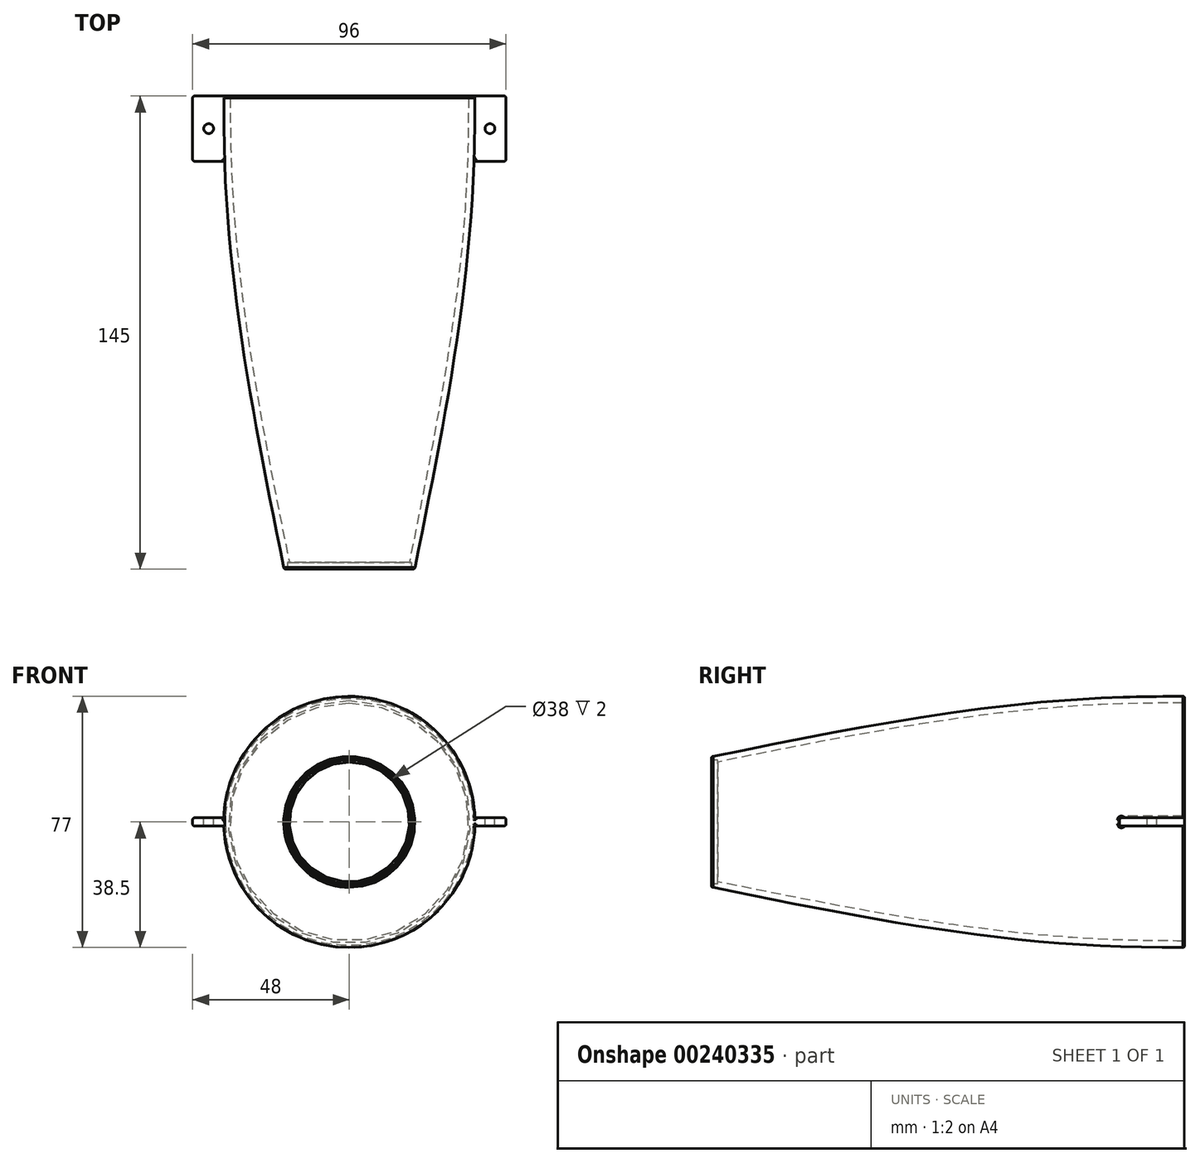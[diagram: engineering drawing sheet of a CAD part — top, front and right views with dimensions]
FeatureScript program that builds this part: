
annotation { "Feature Type Name" : "Feature", "Feature Type Description" : "" }
export const myFeature = defineFeature(function(context is Context, id is Id, definition is map)
    precondition{}
    {
        {
            var Q0;
            Q0=qCreatedBy(makeId("Front.planeOp"),FACE);
            var sketch = newSketch(context, id + "F0", { "sketchPlane" : qUnion([Q0])});
            skCircle(sketch, "E0", {"center": v(0, 0) * mm, "radius": 38.5 * mm});
            skSolve(sketch);
        }
        {
            var Q0;
            Q0=qCreatedBy(makeId("Front.planeOp"),FACE);
            cPlane(context, id + "F1", {"entities" : qUnion([Q0]), "cplaneType" : CPlaneType.OFFSET, "offset" : 20 * mm, "width" : 150 * mm, "height" : 150 * mm});
        }
        {
            var Q0;
            Q0=qCreatedBy(id+"F1.planeOp",FACE);
            var sketch = newSketch(context, id + "F2", { "sketchPlane" : qUnion([Q0])});
            skCircle(sketch, "E1", {"center": v(0, 0) * mm, "radius": 38.2 * mm});
            skSolve(sketch);
        }
        {
            var Q0;
            Q0=qCreatedBy(id+"F1.planeOp",FACE);
            cPlane(context, id + "F3", {"entities" : qUnion([Q0]), "cplaneType" : CPlaneType.OFFSET, "offset" : 125 * mm, "width" : 150 * mm, "height" : 150 * mm});
        }
        {
            var Q0;
            Q0=qCreatedBy(id+"F3.planeOp",FACE);
            var sketch = newSketch(context, id + "F4", { "sketchPlane" : qUnion([Q0])});
            skCircle(sketch, "E2", {"center": v(0, 0) * mm, "radius": 20 * mm});
            skSolve(sketch);
        }
        {
            var Q0;
            Q0 = qSketchRegion(id + "F0", true);
            var Q1;
            Q1 = qSketchRegion(id + "F2", true);
            var Q2;
            Q2 = qSketchRegion(id + "F4", true);
            loft(context, id + "F5", {"sheetProfilesArray" : [{ "sheetProfileEntities" : qUnion([Q0]) }, { "sheetProfileEntities" : qUnion([Q1]) }, { "sheetProfileEntities" : qUnion([Q2]) }]});
        }
        {
            var Q0;
            Q0=makeQuery(id+"F5.opLoft","CAP_FACE",FACE,{"disambiguationData":[OSD([makeQuery(id+"F0.imprint","IMPRINT",FACE,{"disambiguationData":[TD([[makeQuery(id+"F0.imprint","IMPRINT",EDGE,{"derivedFrom":sQuery(id+"F0.wireOp",EDGE,"E0")}),1.0]])]})])],"isStart":true});
            shell(context, id + "F6", {"entities" : qUnion([Q0]), "thickness" : 2 * mm});
        }
        {
            var Q0;
            Q0=makeQuery(id+"F5.opLoft","CAP_FACE",FACE,{"disambiguationData":[OSD([makeQuery(id+"F4.imprint","IMPRINT",FACE,{"disambiguationData":[TD([[makeQuery(id+"F4.imprint","IMPRINT",EDGE,{"derivedFrom":sQuery(id+"F4.wireOp",EDGE,"E2")}),1.0]])]})])],"isStart":true});
            var sketch = newSketch(context, id + "F7", { "sketchPlane" : qUnion([Q0])});
            skCircle(sketch, "E3", {"center": v(0, 0) * mm, "radius": 19 * mm});
            skSolve(sketch);
        }
        {
            var Q0;
            Q0 = qSketchRegion(id + "F7", true);
            extrude(context, id + "F8", {"entities" : qUnion([Q0]), "operationType" : NewBodyOperationType.REMOVE, "oppositeDirection" : true, "depth" : 2 * mm});
        }
        {
            var Q0;
            Q0=qCreatedBy(makeId("Right.planeOp"),FACE);
            cPlane(context, id + "F9", {"entities" : qUnion([Q0]), "cplaneType" : CPlaneType.OFFSET, "offset" : 38 * mm, "width" : 150 * mm, "height" : 150 * mm});
        }
        {
            var Q0;
            Q0=qCreatedBy(makeId("Right.planeOp"),FACE);
            cPlane(context, id + "F10", {"entities" : qUnion([Q0]), "cplaneType" : CPlaneType.OFFSET, "offset" : 38 * mm, "oppositeDirection" : true, "width" : 150 * mm, "height" : 150 * mm});
        }
        {
            var Q0;
            Q0=qCreatedBy(id+"F10.planeOp",FACE);
            var sketch = newSketch(context, id + "F11", { "sketchPlane" : qUnion([Q0])});
            skLineSegment(sketch, "E4.bottom", {"start": v(0, 1.25) * mm, "end": v(-20, 1.25) * mm});
            skLineSegment(sketch, "E4.top", {"start": v(0, -1.25) * mm, "end": v(-20, -1.25) * mm});
            skLineSegment(sketch, "E4.left", {"start": v(0, 1.25) * mm, "end": v(0, -1.25) * mm});
            skLineSegment(sketch, "E4.right", {"start": v(-20, 1.25) * mm, "end": v(-20, -1.25) * mm});
            skSolve(sketch);
        }
        {
            var Q0;
            Q0 = qSketchRegion(id + "F11", true);
            extrude(context, id + "F12", {"entities" : qUnion([Q0]), "operationType" : NewBodyOperationType.ADD, "oppositeDirection" : true, "depth" : 10 * mm});
        }
        {
            var Q0;
            Q0=qCreatedBy(id+"F9.planeOp",FACE);
            var sketch = newSketch(context, id + "F13", { "sketchPlane" : qUnion([Q0])});
            skLineSegment(sketch, "E5.bottom", {"start": v(-20, 1.25) * mm, "end": v(0, 1.25) * mm});
            skLineSegment(sketch, "E5.top", {"start": v(-20, -1.25) * mm, "end": v(0, -1.25) * mm});
            skLineSegment(sketch, "E5.left", {"start": v(-20, 1.25) * mm, "end": v(-20, -1.25) * mm});
            skLineSegment(sketch, "E5.right", {"start": v(0, 1.25) * mm, "end": v(0, -1.25) * mm});
            skSolve(sketch);
        }
        {
            var Q0;
            Q0 = qSketchRegion(id + "F13", true);
            extrude(context, id + "F14", {"entities" : qUnion([Q0]), "operationType" : NewBodyOperationType.ADD, "depth" : 10 * mm});
        }
        {
            var Q0;
            Q0=makeQuery(id+"F12.opExtrude","SWEPT_FACE",FACE,{"disambiguationData":[OSD([sQuery(id+"F11.wireOp",EDGE,"E4.bottom")])]});
            var sketch = newSketch(context, id + "F15", { "sketchPlane" : qUnion([Q0])});
            skCircle(sketch, "E6", {"center": v(-43.09, -10) * mm, "radius": 1.5 * mm});
            skPoint(sketch, "E6.centerSnap0", {"position": v(-43.09, -20) * mm});
            skLineSegment(sketch, "E7", {"start": v(-38.48, 0) * mm, "end": v(-48, -20) * mm, "construction": true});
            skLineSegment(sketch, "E8", {"start": v(-48, 0) * mm, "end": v(-38.18, -20) * mm, "construction": true});
            skCircle(sketch, "E9.MirrorC", {"center": v(43.09, -10) * mm, "radius": 1.5 * mm});
            skSolve(sketch);
        }
        {
            var Q0;
            Q0 = qSketchRegion(id + "F15", true);
            extrude(context, id + "F16", {"entities" : qUnion([Q0]), "operationType" : NewBodyOperationType.REMOVE, "endBound" : BoundingType.THROUGH_ALL, "oppositeDirection" : true, "depth" : 25 * mm});
        }
        {
            var Q0;
            Q0=makeQuery(id+"F6.opShell","OFFSET_EDGE",EDGE,{"disambiguationData":[OSD([sQuery(id+"F0.wireOp",EDGE,"E0")])]});
            var Q1;
            {var subQ0=sQuery(id+"F0.wireOp",EDGE,"E0");Q1=makeQuery(id+"F14.boolean.opBoolean","SPLIT",EDGE,{"disambiguationData":[TD([makeQuery(id+"F12.opExtrude","SWEPT_FACE",FACE,{"disambiguationData":[OSD([sQuery(id+"F11.wireOp",EDGE,"E4.bottom")])]})])],"derivedFrom":makeQuery(id+"F5.opLoft","MID_CAP_EDGE",EDGE,{"disambiguationData":[OSD([subQ0])],"capPos":0.0})});}
            var Q2;
            {var subQ0=sQuery(id+"F0.wireOp",EDGE,"E0");Q2=makeQuery(id+"F14.boolean.opBoolean","SPLIT",EDGE,{"disambiguationData":[TD([makeQuery(id+"F12.opExtrude","SWEPT_FACE",FACE,{"disambiguationData":[OSD([sQuery(id+"F11.wireOp",EDGE,"E4.top")])]})])],"derivedFrom":makeQuery(id+"F5.opLoft","MID_CAP_EDGE",EDGE,{"disambiguationData":[OSD([subQ0])],"capPos":0.0})});}
            var Q3;
            Q3=makeQuery(id+"F14.opExtrude","SWEPT_EDGE",EDGE,{"disambiguationData":[OSD([sQuery(id+"F13.wireOp",EDGE,"E5.top"),sQuery(id+"F13.wireOp",EDGE,"E5.right")])]});
            var Q4;
            Q4=makeQuery(id+"F14.opExtrude","SWEPT_EDGE",EDGE,{"disambiguationData":[OSD([sQuery(id+"F13.wireOp",EDGE,"E5.bottom"),sQuery(id+"F13.wireOp",EDGE,"E5.right")])]});
            var Q5;
            Q5=makeQuery(id+"F14.opExtrude","CAP_EDGE",EDGE,{"disambiguationData":[OSD([sQuery(id+"F13.wireOp",EDGE,"E5.top")])],"isStart":false});
            var Q6;
            Q6=makeQuery(id+"F14.opExtrude","CAP_EDGE",EDGE,{"disambiguationData":[OSD([sQuery(id+"F13.wireOp",EDGE,"E5.bottom")])],"isStart":false});
            var Q7;
            Q7=makeQuery(id+"F14.opExtrude","CAP_EDGE",EDGE,{"disambiguationData":[OSD([sQuery(id+"F13.wireOp",EDGE,"E5.right")])],"isStart":false});
            var Q8;
            Q8=makeQuery(id+"F14.opExtrude","CAP_EDGE",EDGE,{"disambiguationData":[OSD([sQuery(id+"F13.wireOp",EDGE,"E5.left")])],"isStart":false});
            var Q9;
            Q9=makeQuery(id+"F14.opExtrude","SWEPT_EDGE",EDGE,{"disambiguationData":[OSD([sQuery(id+"F13.wireOp",EDGE,"E5.top"),sQuery(id+"F13.wireOp",EDGE,"E5.left")])]});
            var Q10;
            Q10=makeQuery(id+"F14.opExtrude","SWEPT_EDGE",EDGE,{"disambiguationData":[OSD([sQuery(id+"F13.wireOp",EDGE,"E5.bottom"),sQuery(id+"F13.wireOp",EDGE,"E5.left")])]});
            var Q11;
            Q11=makeQuery(id+"F14.boolean.opBoolean","INTERSECT",EDGE,{"derivedFrom":[makeQuery(id+"F5.opLoft","SWEPT_FACE",FACE,{"disambiguationData":[OSD([sQuery(id+"F0.wireOp",EDGE,"E0"),sQuery(id+"F2.wireOp",EDGE,"E1")])]}),makeQuery(id+"F14.opExtrude","SWEPT_FACE",FACE,{"disambiguationData":[OSD([sQuery(id+"F13.wireOp",EDGE,"E5.left")])]})]});
            var Q12;
            Q12=makeQuery(id+"F12.opExtrude","SWEPT_EDGE",EDGE,{"disambiguationData":[OSD([sQuery(id+"F11.wireOp",EDGE,"E4.top"),sQuery(id+"F11.wireOp",EDGE,"E4.left")])]});
            var Q13;
            Q13=makeQuery(id+"F12.opExtrude","SWEPT_EDGE",EDGE,{"disambiguationData":[OSD([sQuery(id+"F11.wireOp",EDGE,"E4.bottom"),sQuery(id+"F11.wireOp",EDGE,"E4.left")])]});
            var Q14;
            Q14=makeQuery(id+"F12.opExtrude","CAP_EDGE",EDGE,{"disambiguationData":[OSD([sQuery(id+"F11.wireOp",EDGE,"E4.left")])],"isStart":false});
            var Q15;
            Q15=makeQuery(id+"F12.opExtrude","CAP_EDGE",EDGE,{"disambiguationData":[OSD([sQuery(id+"F11.wireOp",EDGE,"E4.top")])],"isStart":false});
            var Q16;
            Q16=makeQuery(id+"F12.opExtrude","CAP_EDGE",EDGE,{"disambiguationData":[OSD([sQuery(id+"F11.wireOp",EDGE,"E4.bottom")])],"isStart":false});
            var Q17;
            Q17=makeQuery(id+"F12.opExtrude","CAP_EDGE",EDGE,{"disambiguationData":[OSD([sQuery(id+"F11.wireOp",EDGE,"E4.right")])],"isStart":false});
            var Q18;
            Q18=makeQuery(id+"F12.opExtrude","SWEPT_EDGE",EDGE,{"disambiguationData":[OSD([sQuery(id+"F11.wireOp",EDGE,"E4.bottom"),sQuery(id+"F11.wireOp",EDGE,"E4.right")])]});
            var Q19;
            Q19=makeQuery(id+"F12.boolean.opBoolean","INTERSECT",EDGE,{"derivedFrom":[makeQuery(id+"F5.opLoft","SWEPT_FACE",FACE,{"disambiguationData":[OSD([sQuery(id+"F0.wireOp",EDGE,"E0"),sQuery(id+"F2.wireOp",EDGE,"E1")])]}),makeQuery(id+"F12.opExtrude","SWEPT_FACE",FACE,{"disambiguationData":[OSD([sQuery(id+"F11.wireOp",EDGE,"E4.bottom")])]})]});
            var Q20;
            Q20=makeQuery(id+"F12.opExtrude","SWEPT_EDGE",EDGE,{"disambiguationData":[OSD([sQuery(id+"F11.wireOp",EDGE,"E4.top"),sQuery(id+"F11.wireOp",EDGE,"E4.right")])]});
            var Q21;
            Q21=makeQuery(id+"F5.opLoft","MID_CAP_EDGE",EDGE,{"disambiguationData":[OSD([sQuery(id+"F0.wireOp",EDGE,"E0"),sQuery(id+"F4.wireOp",EDGE,"E2")])],"capPos":2.0});
            var Q22;
            Q22=makeQuery(id+"F6.opShell","OFFSET_EDGE",EDGE,{"disambiguationData":[OSD([sQuery(id+"F0.wireOp",EDGE,"E0"),sQuery(id+"F4.wireOp",EDGE,"E2")])]});
            fillet(context, id + "F17", {"entities" : qUnion([Q0, Q1, Q2, Q3, Q4, Q5, Q6, Q7, Q8, Q9, Q10, Q11, Q12, Q13, Q14, Q15, Q16, Q17, Q18, Q19, Q20, Q21, Q22]), "radius" : .6 * mm, "tangentPropagation" : true, "allowEdgeOverflow" : false});
        }
    });
